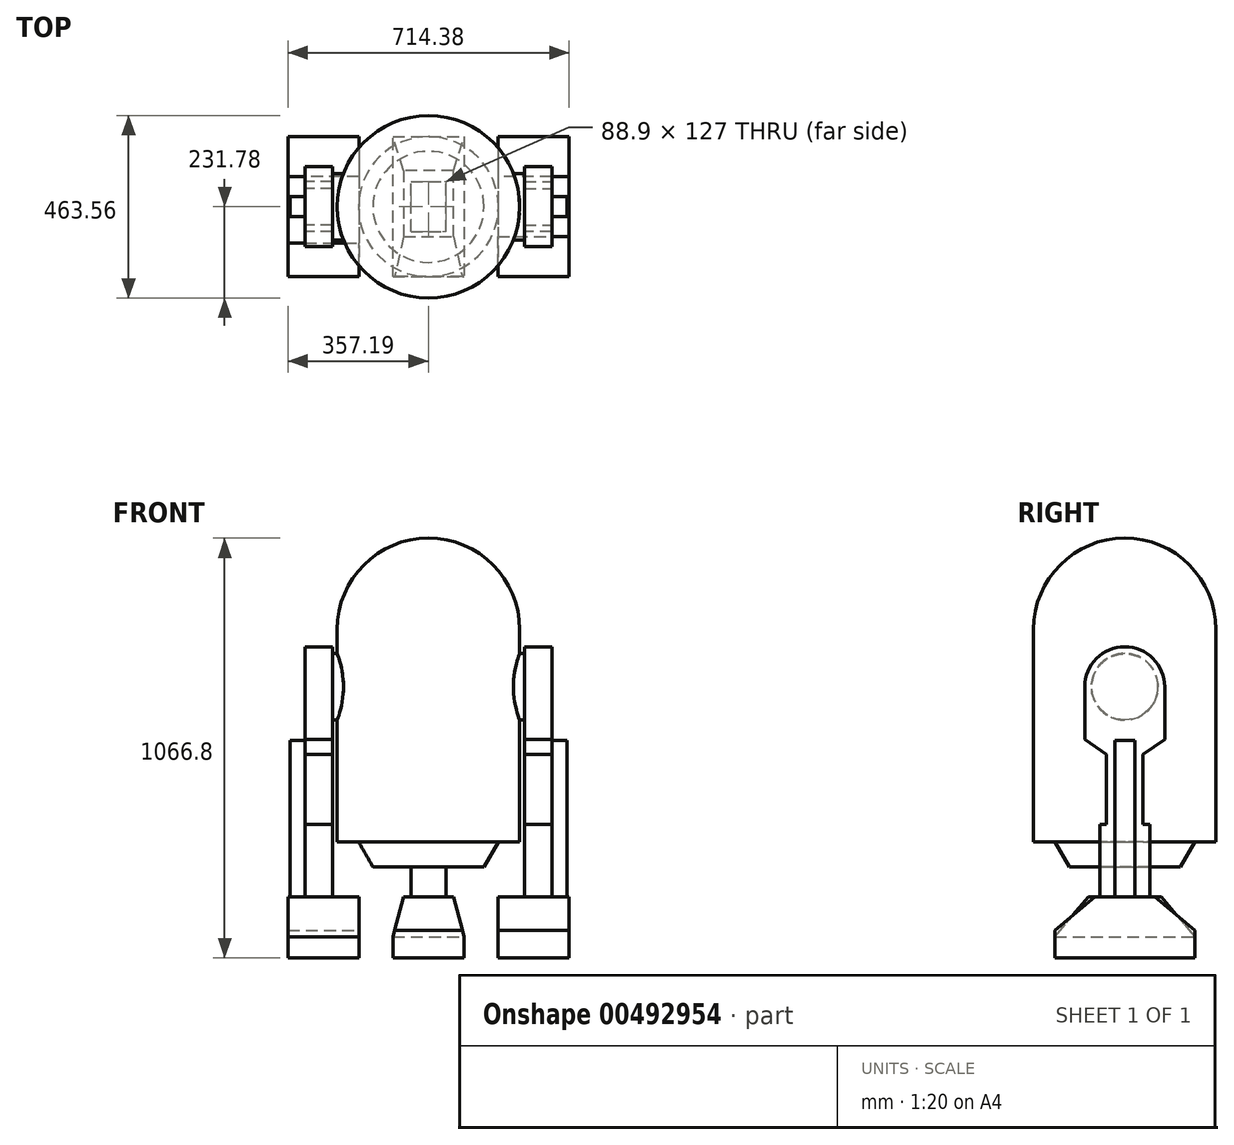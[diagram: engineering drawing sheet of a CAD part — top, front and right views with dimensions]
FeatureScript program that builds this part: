
annotation { "Feature Type Name" : "Feature", "Feature Type Description" : "" }
export const myFeature = defineFeature(function(context is Context, id is Id, definition is map)
    precondition{}
    {
        {
            var Q0;
            Q0=qCreatedBy(makeId("Top.planeOp"),FACE);
            var sketch = newSketch(context, id + "F0", { "sketchPlane" : qUnion([Q0])});
            skCircle(sketch, "E0", {"center": v(0, 0) * mm, "radius": 231.78 * mm});
            skLineSegment(sketch, "E1.bottom", {"start": v(243.68, 84.58) * mm, "end": v(215.8, 84.58) * mm});
            skLineSegment(sketch, "E1.top", {"start": v(243.68, -84.58) * mm, "end": v(215.8, -84.58) * mm});
            skLineSegment(sketch, "E1.left", {"start": v(243.68, 84.58) * mm, "end": v(243.68, -84.58) * mm});
            skLineSegment(sketch, "E1.right", {"start": v(-243.68, 84.58) * mm, "end": v(-243.68, -84.58) * mm});
            skLineSegment(sketch, "E2.bottom", {"start": v(313.53, 101.6) * mm, "end": v(243.68, 101.6) * mm});
            skLineSegment(sketch, "E2.top", {"start": v(313.53, -101.6) * mm, "end": v(243.68, -101.6) * mm});
            skLineSegment(sketch, "E2.left", {"start": v(313.53, 101.6) * mm, "end": v(313.53, -101.6) * mm});
            skLineSegment(sketch, "E2.right", {"start": v(243.68, 101.6) * mm, "end": v(243.68, -101.6) * mm});
            skPoint(sketch, "E2.middle", {"position": v(278.6, 0) * mm});
            skLineSegment(sketch, "E3.bottom", {"start": v(338.93, -50.8) * mm, "end": v(313.53, -50.8) * mm});
            skLineSegment(sketch, "E3.top", {"start": v(338.93, 50.8) * mm, "end": v(313.53, 50.8) * mm});
            skLineSegment(sketch, "E3.left", {"start": v(338.93, -50.8) * mm, "end": v(338.93, 50.8) * mm});
            skLineSegment(sketch, "E3.right", {"start": v(313.53, -50.8) * mm, "end": v(313.53, 50.8) * mm});
            skPoint(sketch, "E3.middle", {"position": v(326.23, 0) * mm});
            skLineSegment(sketch, "E4.trimOffspring", {"start": v(-215.8, 84.58) * mm, "end": v(-243.68, 84.58) * mm});
            skLineSegment(sketch, "E5.trimOffspring", {"start": v(-215.8, -84.58) * mm, "end": v(-243.68, -84.58) * mm});
            skLineSegment(sketch, "E6.MirrorCS", {"start": v(-243.68, 101.6) * mm, "end": v(-243.68, -101.6) * mm});
            skLineSegment(sketch, "E7.MirrorCS", {"start": v(-313.53, 101.6) * mm, "end": v(-243.68, 101.6) * mm});
            skLineSegment(sketch, "E8.MirrorCS", {"start": v(-313.53, -101.6) * mm, "end": v(-243.68, -101.6) * mm});
            skLineSegment(sketch, "E9.MirrorCS", {"start": v(-313.53, 101.6) * mm, "end": v(-313.53, -101.6) * mm});
            skLineSegment(sketch, "E10.MirrorCS", {"start": v(-338.93, -50.8) * mm, "end": v(-313.53, -50.8) * mm});
            skLineSegment(sketch, "E11.MirrorCS", {"start": v(-338.93, -50.8) * mm, "end": v(-338.93, 50.8) * mm});
            skLineSegment(sketch, "E12.MirrorCS", {"start": v(-338.93, 50.8) * mm, "end": v(-313.53, 50.8) * mm});
            skLineSegment(sketch, "E13", {"start": v(0, 0) * mm, "end": v(0, 231.78) * mm});
            skLineSegment(sketch, "E14", {"start": v(0, 0) * mm, "end": v(0, -231.78) * mm});
            skLineSegment(sketch, "E15", {"start": v(313.53, 0) * mm, "end": v(243.68, 0) * mm});
            skLineSegment(sketch, "E16", {"start": v(-243.68, 0) * mm, "end": v(-313.53, 0) * mm});
            skSolve(sketch);
        }
        {
            var Q0;
            {var subQ0=sQuery(id+"F0.wireOp",EDGE,"E0");var subQ1=makeQuery(id+"F0.imprint","INTERSECT",VERTEX,{"derivedFrom":[subQ0,sQuery(id+"F0.wireOp",EDGE,"E1.bottom")]});Q0=makeQuery(id+"F0.imprint","IMPRINT",FACE,{"disambiguationData":[TD([[makeQuery(id+"F0.imprint","IMPRINT",EDGE,{"disambiguationData":[TD([[subQ1,-1.0]])],"derivedFrom":subQ0}),1.0]])]});}
            var Q1;
            {var subQ3=sQuery(id+"F0.wireOp",EDGE,"E13");Q1=makeQuery(id+"F0.imprint","IMPRINT",FACE,{"disambiguationData":[TD([[makeQuery(id+"F0.imprint","IMPRINT",EDGE,{"derivedFrom":subQ3}),1.0]])]});}
            extrude(context, id + "F1", {"entities" : qUnion([Q0, Q1]), "oppositeDirection" : true, "depth" : 539.75 * mm});
        }
        {
            var Q0;
            {var subQ0=sQuery(id+"F0.wireOp",EDGE,"E13");Q0=makeQuery(id+"F0.imprint","IMPRINT",FACE,{"disambiguationData":[TD([[makeQuery(id+"F0.imprint","IMPRINT",EDGE,{"derivedFrom":subQ0}),-1.0]])]});}
            var Q1;
            Q1=sQuery(id+"F0.wireOp",EDGE,"E14");
            revolve(context, id + "F2", {"operationType" : NewBodyOperationType.ADD, "entities" : qUnion([Q0]), "axis" : qUnion([Q1]), "revolveType" : RevolveType.ONE_DIRECTION, "angle" : 180 * degree});
        }
        {
            var Q0;
            {var subQ2=sQuery(id+"F0.wireOp",EDGE,"E2.top");Q0=makeQuery(id+"F0.imprint","IMPRINT",FACE,{"disambiguationData":[TD([[makeQuery(id+"F0.imprint","IMPRINT",EDGE,{"derivedFrom":subQ2}),-1.0]])]});}
            var Q1;
            {var subQ2=sQuery(id+"F0.wireOp",EDGE,"E2.bottom");Q1=makeQuery(id+"F0.imprint","IMPRINT",FACE,{"disambiguationData":[TD([[makeQuery(id+"F0.imprint","IMPRINT",EDGE,{"derivedFrom":subQ2}),1.0]])]});}
            extrude(context, id + "F3", {"entities" : qUnion([Q0, Q1]), "oppositeDirection" : true, "depth" : 714.38 * mm, "hasSecondDirection" : true, "secondDirectionOppositeDirection" : true, "secondDirectionDepth" : 146.05 * mm});
        }
        {
            var Q0;
            Q0=makeQuery(id+"F3.opExtrude","CAP_FACE",FACE,{"disambiguationData":[OSD([sQuery(id+"F0.wireOp",EDGE,"E2.bottom"),sQuery(id+"F0.wireOp",EDGE,"E2.top"),sQuery(id+"F0.wireOp",EDGE,"E2.left"),sQuery(id+"F0.wireOp",EDGE,"E2.right"),sQuery(id+"F0.wireOp",EDGE,"E3.right")])],"isStart":true});
            var sketch = newSketch(context, id + "F4", { "sketchPlane" : qUnion([Q0])});
            skLineSegment(sketch, "E17", {"start": v(313.53, 0) * mm, "end": v(243.68, 0) * mm});
            skSolve(sketch);
        }
        {
            var Q0;
            {var subQ0=sQuery(id+"F4.wireOp",EDGE,"E17");Q0=makeQuery(id+"F4.imprint","IMPRINT",FACE,{"disambiguationData":[TD([[makeQuery(id+"F4.imprint","IMPRINT",EDGE,{"derivedFrom":subQ0}),1.0]])]});}
            var Q1;
            Q1=sQuery(id+"F4.wireOp",EDGE,"E17");
            revolve(context, id + "F5", {"operationType" : NewBodyOperationType.ADD, "entities" : qUnion([Q0]), "axis" : qUnion([Q1]), "revolveType" : RevolveType.FULL});
        }
        {
            var Q0;
            {var subQ0=sQuery(id+"F0.wireOp",EDGE,"E3.right");var subQ1=sQuery(id+"F0.wireOp",EDGE,"E2.left");Q0=makeQuery(id+"F5.boolean.opBoolean","MERGE",FACE,{"derivedFrom":[makeQuery(id+"F3.opExtrude","SWEPT_FACE",FACE,{"disambiguationData":[OSD([subQ1,subQ0])]}),makeQuery(id+"F5.opRevolve","SWEPT_FACE",FACE,{"disambiguationData":[OSD([subQ1,subQ0])]})]});}
            var sketch = newSketch(context, id + "F6", { "sketchPlane" : qUnion([Q0])});
            skCircle(sketch, "E18", {"center": v(0, -146.05) * mm, "radius": 84.58 * mm});
            skLineSegment(sketch, "E19.bottom", {"start": v(46.04, -317.5) * mm, "end": v(-46.04, -317.5) * mm, "construction": true});
            skLineSegment(sketch, "E19.left", {"start": v(46.04, -317.5) * mm, "end": v(46.04, -495.3) * mm});
            skLineSegment(sketch, "E19.right", {"start": v(-46.04, -317.5) * mm, "end": v(-46.04, -495.3) * mm});
            skPoint(sketch, "E19.middle", {"position": v(0, -406.4) * mm});
            skLineSegment(sketch, "E20", {"start": v(-101.6, -279.4) * mm, "end": v(-46.04, -317.5) * mm});
            skLineSegment(sketch, "E21", {"start": v(101.6, -279.4) * mm, "end": v(46.04, -317.5) * mm});
            skLineSegment(sketch, "E22.bottom", {"start": v(63.5, -495.3) * mm, "end": v(46.04, -495.3) * mm});
            skLineSegment(sketch, "E22.top", {"start": v(63.5, -714.38) * mm, "end": v(-63.5, -714.38) * mm});
            skLineSegment(sketch, "E22.left", {"start": v(63.5, -495.3) * mm, "end": v(63.5, -714.38) * mm});
            skLineSegment(sketch, "E22.right", {"start": v(-63.5, -495.3) * mm, "end": v(-63.5, -714.38) * mm});
            skPoint(sketch, "E22.middle", {"position": v(0, -604.84) * mm});
            skLineSegment(sketch, "E23.trimOffspring", {"start": v(-46.04, -495.3) * mm, "end": v(-63.5, -495.3) * mm});
            skSolve(sketch);
        }
        {
            var Q0;
            Q0=makeQuery(id+"F6.imprint","IMPRINT",FACE,{"disambiguationData":[TD([[makeQuery(id+"F6.imprint","IMPRINT",EDGE,{"derivedFrom":sQuery(id+"F6.wireOp",EDGE,"E19.left")}),1.0]])]});
            var Q1;
            Q1=makeQuery(id+"F6.imprint","IMPRINT",FACE,{"disambiguationData":[TD([[makeQuery(id+"F6.imprint","IMPRINT",EDGE,{"derivedFrom":sQuery(id+"F6.wireOp",EDGE,"E19.right")}),-1.0]])]});
            var Q2;
            {var subQ0=sQuery(id+"F0.wireOp",EDGE,"E2.right");Q2=makeQuery(id+"F5.boolean.opBoolean","MERGE",FACE,{"derivedFrom":[makeQuery(id+"F3.opExtrude","SWEPT_FACE",FACE,{"disambiguationData":[OSD([subQ0])]}),makeQuery(id+"F5.opRevolve","SWEPT_FACE",FACE,{"disambiguationData":[OSD([subQ0])]})]});}
            extrude(context, id + "F7", {"entities" : qUnion([Q0, Q1]), "operationType" : NewBodyOperationType.REMOVE, "endBound" : BoundingType.UP_TO_SURFACE, "oppositeDirection" : true, "endBoundEntityFace" : qUnion([Q2]), "depth" : 25.4 * mm});
        }
        {
            var Q0;
            Q0=makeQuery(id+"F6.imprint","IMPRINT",FACE,{"disambiguationData":[TD([[makeQuery(id+"F6.imprint","IMPRINT",EDGE,{"derivedFrom":sQuery(id+"F6.wireOp",EDGE,"E18")}),-1.0]])]});
            var sketch = newSketch(context, id + "F8", { "sketchPlane" : qUnion([Q0])});
            skLineSegment(sketch, "E24.bottom", {"start": v(25.4, -282.58) * mm, "end": v(-25.4, -282.58) * mm});
            skLineSegment(sketch, "E24.top", {"start": v(25.4, -714.38) * mm, "end": v(-25.4, -714.38) * mm});
            skLineSegment(sketch, "E24.left", {"start": v(25.4, -282.58) * mm, "end": v(25.4, -714.38) * mm});
            skLineSegment(sketch, "E24.right", {"start": v(-25.4, -282.58) * mm, "end": v(-25.4, -714.38) * mm});
            skPoint(sketch, "E24.middle", {"position": v(0, -498.48) * mm});
            skSolve(sketch);
        }
        {
            var Q0;
            Q0=makeQuery(id+"F8.imprint","IMPRINT",FACE,{"disambiguationData":[TD([[makeQuery(id+"F8.imprint","IMPRINT",EDGE,{"derivedFrom":sQuery(id+"F8.wireOp",EDGE,"E24.bottom")}),1.0]])]});
            extrude(context, id + "F9", {"entities" : qUnion([Q0]), "operationType" : NewBodyOperationType.ADD, "depth" : 38.1 * mm});
        }
        {
            var Q0;
            Q0=makeQuery(id+"F3.opExtrude","SWEPT_BODY",BODY,{"disambiguationData":[OSD([sQuery(id+"F0.wireOp",EDGE,"E2.bottom"),sQuery(id+"F0.wireOp",EDGE,"E2.top"),sQuery(id+"F0.wireOp",EDGE,"E2.left"),sQuery(id+"F0.wireOp",EDGE,"E2.right"),sQuery(id+"F0.wireOp",EDGE,"E3.right")])]});
            var Q1;
            Q1=qCreatedBy(makeId("Right.planeOp"),FACE);
            mirror(context, id + "F10", {"entities" : qUnion([Q0]), "mirrorPlane" : qUnion([Q1])});
        }
        {
            var Q0;
            Q0=makeQuery(id+"F6.imprint","IMPRINT",FACE,{"disambiguationData":[TD([[makeQuery(id+"F6.imprint","IMPRINT",EDGE,{"derivedFrom":sQuery(id+"F6.wireOp",EDGE,"E18")}),1.0]])]});
            var Q1;
            Q1=sQuery(id+"F6.wireOp",EDGE,"E18");
            var Q2;
            {var subQ0=sQuery(id+"F0.wireOp",EDGE,"E3.right");var subQ1=sQuery(id+"F0.wireOp",EDGE,"E2.left");Q2=makeQuery(id+"F10.opPattern","COPY",FACE,{"derivedFrom":makeQuery(id+"F5.boolean.opBoolean","MERGE",FACE,{"derivedFrom":[makeQuery(id+"F3.opExtrude","SWEPT_FACE",FACE,{"disambiguationData":[OSD([subQ1,subQ0])]}),makeQuery(id+"F5.opRevolve","SWEPT_FACE",FACE,{"disambiguationData":[OSD([subQ1,subQ0])]})]}),"instanceName":"1"});}
            extrude(context, id + "F11", {"entities" : qUnion([Q0]), "operationType" : NewBodyOperationType.ADD, "surfaceEntities" : qUnion([Q1]), "endBound" : BoundingType.UP_TO_SURFACE, "oppositeDirection" : true, "endBoundEntityFace" : qUnion([Q2]), "depth" : 25.4 * mm});
        }
        {
            var Q0;
            Q0=makeQuery(id+"F1.opExtrude","CAP_FACE",FACE,{"disambiguationData":[OSD([sQuery(id+"F0.wireOp",EDGE,"E0")])],"isStart":false});
            var sketch = newSketch(context, id + "F12", { "sketchPlane" : qUnion([Q0])});
            skCircle(sketch, "E25", {"center": v(0, 0) * mm, "radius": 177.8 * mm});
            skSolve(sketch);
        }
        {
            var Q0;
            Q0=makeQuery(id+"F12.imprint","IMPRINT",FACE,{"disambiguationData":[TD([[makeQuery(id+"F12.imprint","IMPRINT",EDGE,{"derivedFrom":sQuery(id+"F12.wireOp",EDGE,"E25")}),1.0]])]});
            extrude(context, id + "F13", {"entities" : qUnion([Q0]), "operationType" : NewBodyOperationType.ADD, "depth" : 63.5 * mm});
        }
        {
            var Q0;
            Q0=makeQuery(id+"F13.opExtrude","CAP_EDGE",EDGE,{"disambiguationData":[OSD([sQuery(id+"F12.wireOp",EDGE,"E25")])],"isStart":false});
            chamfer(context, id + "F14", {"entities" : qUnion([Q0]), "chamferType" : ChamferType.OFFSET_ANGLE, "width" : 63.5 * mm, "oppositeDirection" : true, "angle" : 30 * degree, "tangentPropagation" : true});
        }
        {
            var Q0;
            Q0=qCreatedBy(makeId("Top.planeOp"),FACE);
            cPlane(context, id + "F15", {"entities" : qUnion([Q0]), "cplaneType" : CPlaneType.OFFSET, "offset" : 835.02 * mm, "oppositeDirection" : true, "width" : 152.4 * mm, "height" : 152.4 * mm});
        }
        {
            var Q0;
            Q0=qCreatedBy(id+"F15.planeOp",FACE);
            var sketch = newSketch(context, id + "F16", { "sketchPlane" : qUnion([Q0])});
            skLineSegment(sketch, "E26.bottom", {"start": v(-90.49, 177.8) * mm, "end": v(90.49, 177.8) * mm});
            skLineSegment(sketch, "E26.top", {"start": v(-90.49, -177.8) * mm, "end": v(90.49, -177.8) * mm});
            skLineSegment(sketch, "E26.left", {"start": v(-90.49, 177.8) * mm, "end": v(-90.49, -177.8) * mm});
            skLineSegment(sketch, "E26.right", {"start": v(90.49, 177.8) * mm, "end": v(90.49, -177.8) * mm});
            skPoint(sketch, "E26.middle", {"position": v(0, 0) * mm});
            skLineSegment(sketch, "E27.1.0.0", {"start": v(176.21, -177.8) * mm, "end": v(357.19, -177.8) * mm});
            skLineSegment(sketch, "E27.1.0.1", {"start": v(176.21, 177.8) * mm, "end": v(176.21, -177.8) * mm});
            skLineSegment(sketch, "E27.1.0.2", {"start": v(357.19, 177.8) * mm, "end": v(357.19, -177.8) * mm});
            skLineSegment(sketch, "E27.1.0.3", {"start": v(176.21, 177.8) * mm, "end": v(357.19, 177.8) * mm});
            skLineSegment(sketch, "E27.direction1", {"start": v(-90.49, -177.8) * mm, "end": v(176.21, -177.8) * mm, "construction": true});
            skLineSegment(sketch, "E28", {"start": v(266.7, -177.8) * mm, "end": v(266.7, 177.8) * mm, "construction": true});
            skLineSegment(sketch, "E29", {"start": v(0, -177.8) * mm, "end": v(0, 177.8) * mm, "construction": true});
            skLineSegment(sketch, "E30.MirrorCS", {"start": v(-176.21, 177.8) * mm, "end": v(-176.21, -177.8) * mm});
            skLineSegment(sketch, "E31.MirrorCS", {"start": v(-176.21, -177.8) * mm, "end": v(-357.19, -177.8) * mm});
            skLineSegment(sketch, "E32.MirrorCS", {"start": v(-357.19, 177.8) * mm, "end": v(-357.19, -177.8) * mm});
            skLineSegment(sketch, "E33.MirrorCS", {"start": v(-176.21, 177.8) * mm, "end": v(-357.19, 177.8) * mm});
            skSolve(sketch);
        }
        {
            var Q0;
            Q0=makeQuery(id+"F16.imprint","IMPRINT",FACE,{"disambiguationData":[TD([[makeQuery(id+"F16.imprint","IMPRINT",EDGE,{"derivedFrom":sQuery(id+"F16.wireOp",EDGE,"E30.MirrorCS")}),-1.0]])]});
            var Q1;
            Q1=makeQuery(id+"F16.imprint","IMPRINT",FACE,{"disambiguationData":[TD([[makeQuery(id+"F16.imprint","IMPRINT",EDGE,{"derivedFrom":sQuery(id+"F16.wireOp",EDGE,"E26.bottom")}),-1.0]])]});
            var Q2;
            Q2=makeQuery(id+"F16.imprint","IMPRINT",FACE,{"disambiguationData":[TD([[makeQuery(id+"F16.imprint","IMPRINT",EDGE,{"derivedFrom":sQuery(id+"F16.wireOp",EDGE,"E27.1.0.0")}),1.0]])]});
            extrude(context, id + "F17", {"entities" : qUnion([Q0, Q1, Q2]), "operationType" : NewBodyOperationType.ADD, "depth" : 155.57 * mm});
        }
        {
            var Q0;
            Q0=makeQuery(id+"F17.opExtrude","CAP_FACE",FACE,{"disambiguationData":[OSD([sQuery(id+"F16.wireOp",EDGE,"E26.bottom"),sQuery(id+"F16.wireOp",EDGE,"E26.top"),sQuery(id+"F16.wireOp",EDGE,"E26.left"),sQuery(id+"F16.wireOp",EDGE,"E26.right")])],"isStart":false});
            var sketch = newSketch(context, id + "F18", { "sketchPlane" : qUnion([Q0])});
            skLineSegment(sketch, "E34.bottom", {"start": v(44.45, 63.5) * mm, "end": v(-44.45, 63.5) * mm});
            skLineSegment(sketch, "E34.top", {"start": v(44.45, -63.5) * mm, "end": v(-44.45, -63.5) * mm});
            skLineSegment(sketch, "E34.left", {"start": v(44.45, 63.5) * mm, "end": v(44.45, -63.5) * mm});
            skLineSegment(sketch, "E34.right", {"start": v(-44.45, 63.5) * mm, "end": v(-44.45, -63.5) * mm});
            skPoint(sketch, "E34.middle", {"position": v(0, 0) * mm});
            skSolve(sketch);
        }
        {
            var Q0;
            Q0=makeQuery(id+"F18.imprint","IMPRINT",FACE,{"disambiguationData":[TD([[makeQuery(id+"F18.imprint","IMPRINT",EDGE,{"derivedFrom":sQuery(id+"F18.wireOp",EDGE,"E34.bottom")}),1.0]])]});
            var Q1;
            Q1=makeQuery(id+"F13.opExtrude","CAP_FACE",FACE,{"disambiguationData":[OSD([sQuery(id+"F12.wireOp",EDGE,"E25")])],"isStart":false});
            extrude(context, id + "F19", {"entities" : qUnion([Q0]), "operationType" : NewBodyOperationType.ADD, "endBound" : BoundingType.UP_TO_SURFACE, "endBoundEntityFace" : qUnion([Q1]), "depth" : 25.4 * mm});
        }
        {
            var Q0;
            Q0=makeQuery(id+"F17.opExtrude","CAP_EDGE",EDGE,{"disambiguationData":[OSD([sQuery(id+"F16.wireOp",EDGE,"E27.1.0.0")])],"isStart":false});
            var Q1;
            Q1=makeQuery(id+"F17.opExtrude","CAP_EDGE",EDGE,{"disambiguationData":[OSD([sQuery(id+"F16.wireOp",EDGE,"E31.MirrorCS")])],"isStart":false});
            var Q2;
            Q2=makeQuery(id+"F17.opExtrude","CAP_EDGE",EDGE,{"disambiguationData":[OSD([sQuery(id+"F16.wireOp",EDGE,"E33.MirrorCS")])],"isStart":false});
            var Q3;
            Q3=makeQuery(id+"F17.opExtrude","CAP_EDGE",EDGE,{"disambiguationData":[OSD([sQuery(id+"F16.wireOp",EDGE,"E27.1.0.3")])],"isStart":false});
            var Q4;
            Q4=makeQuery(id+"F17.opExtrude","CAP_EDGE",EDGE,{"disambiguationData":[OSD([sQuery(id+"F16.wireOp",EDGE,"E26.bottom")])],"isStart":false});
            var Q5;
            Q5=makeQuery(id+"F17.opExtrude","CAP_EDGE",EDGE,{"disambiguationData":[OSD([sQuery(id+"F16.wireOp",EDGE,"E26.top")])],"isStart":false});
            chamfer(context, id + "F20", {"entities" : qUnion([Q0, Q1, Q2, Q3, Q4, Q5]), "chamferType" : ChamferType.OFFSET_ANGLE, "width" : 101.6 * mm, "oppositeDirection" : false, "angle" : 40 * degree, "tangentPropagation" : true});
        }
        {
            var Q0;
            Q0=makeQuery(id+"F17.opExtrude","CAP_EDGE",EDGE,{"disambiguationData":[OSD([sQuery(id+"F16.wireOp",EDGE,"E26.left")])],"isStart":false});
            var Q1;
            Q1=makeQuery(id+"F17.opExtrude","CAP_EDGE",EDGE,{"disambiguationData":[OSD([sQuery(id+"F16.wireOp",EDGE,"E26.right")])],"isStart":false});
            chamfer(context, id + "F21", {"entities" : qUnion([Q0, Q1]), "chamferType" : ChamferType.OFFSET_ANGLE, "width" : 101.6 * mm, "oppositeDirection" : true, "angle" : 15 * degree});
        }
        {
            var Q0;
            Q0=qCreatedBy(id+"F15.planeOp",FACE);
            var sketch = newSketch(context, id + "F22", { "sketchPlane" : qUnion([Q0])});
            skLineSegment(sketch, "E35.bottom", {"start": v(406.4, -292.1) * mm, "end": v(-406.4, -292.1) * mm});
            skLineSegment(sketch, "E35.top", {"start": v(406.4, 292.1) * mm, "end": v(-406.4, 292.1) * mm});
            skLineSegment(sketch, "E35.left", {"start": v(406.4, -292.1) * mm, "end": v(406.4, 292.1) * mm});
            skLineSegment(sketch, "E35.right", {"start": v(-406.4, -292.1) * mm, "end": v(-406.4, 292.1) * mm});
            skPoint(sketch, "E35.middle", {"position": v(0, 0) * mm});
            skLineSegment(sketch, "E36", {"start": v(-406.4, -228.6) * mm, "end": v(-368.3, -228.6) * mm});
            skLineSegment(sketch, "E37", {"start": v(-368.3, -228.6) * mm, "end": v(-368.3, -292.1) * mm});
            skLineSegment(sketch, "E38", {"start": v(0, -292.1) * mm, "end": v(0, 292.1) * mm, "construction": true});
            skLineSegment(sketch, "E39", {"start": v(406.4, 0) * mm, "end": v(-406.4, 0) * mm, "construction": true});
            skLineSegment(sketch, "E40.MirrorCS", {"start": v(368.3, -228.6) * mm, "end": v(368.3, -292.1) * mm});
            skLineSegment(sketch, "E41.MirrorCS", {"start": v(406.4, -228.6) * mm, "end": v(368.3, -228.6) * mm});
            skLineSegment(sketch, "E42.MirrorCS", {"start": v(-406.4, 228.6) * mm, "end": v(-368.3, 228.6) * mm});
            skLineSegment(sketch, "E43.MirrorCS", {"start": v(-368.3, 228.6) * mm, "end": v(-368.3, 292.1) * mm});
            skLineSegment(sketch, "E44.MirrorCS", {"start": v(406.4, 228.6) * mm, "end": v(368.3, 228.6) * mm});
            skLineSegment(sketch, "E45.MirrorCS", {"start": v(368.3, 228.6) * mm, "end": v(368.3, 292.1) * mm});
            skLineSegment(sketch, "E46", {"start": v(368.3, 285.75) * mm, "end": v(-368.3, 285.75) * mm});
            skLineSegment(sketch, "E47", {"start": v(-400.05, 228.6) * mm, "end": v(-400.05, -228.6) * mm});
            skLineSegment(sketch, "E48", {"start": v(-135.56, 292.1) * mm, "end": v(-135.56, 285.75) * mm, "construction": true});
            skLineSegment(sketch, "E49", {"start": v(-400.05, 178.52) * mm, "end": v(-406.4, 178.52) * mm, "construction": true});
            skLineSegment(sketch, "E50.MirrorCS", {"start": v(368.3, -285.75) * mm, "end": v(-368.3, -285.75) * mm});
            skLineSegment(sketch, "E51.MirrorCS", {"start": v(400.05, 228.6) * mm, "end": v(400.05, -228.6) * mm});
            skSolve(sketch);
        }
        {
            var Q0;
            {var subQ4=sQuery(id+"F22.wireOp",EDGE,"E44.MirrorCS");Q0=makeQuery(id+"F22.imprint","IMPRINT",FACE,{"disambiguationData":[TD([[makeQuery(id+"F22.imprint","IMPRINT",EDGE,{"derivedFrom":subQ4}),-1.0]])]});}
            var Q1;
            {var subQ3=sQuery(id+"F22.wireOp",EDGE,"E40.MirrorCS");Q1=makeQuery(id+"F22.imprint","IMPRINT",FACE,{"disambiguationData":[TD([[makeQuery(id+"F22.imprint","IMPRINT",EDGE,{"derivedFrom":subQ3}),1.0]])]});}
            var Q2;
            {var subQ4=sQuery(id+"F22.wireOp",EDGE,"E42.MirrorCS");Q2=makeQuery(id+"F22.imprint","IMPRINT",FACE,{"disambiguationData":[TD([[makeQuery(id+"F22.imprint","IMPRINT",EDGE,{"derivedFrom":subQ4}),1.0]])]});}
            var Q3;
            {var subQ4=sQuery(id+"F22.wireOp",EDGE,"E36");Q3=makeQuery(id+"F22.imprint","IMPRINT",FACE,{"disambiguationData":[TD([[makeQuery(id+"F22.imprint","IMPRINT",EDGE,{"derivedFrom":subQ4}),-1.0]])]});}
            extrude(context, id + "F23", {"entities" : qUnion([Q0, Q1, Q2, Q3]), "depth" : 1136.65 * mm, "hasSecondDirection" : true, "secondDirectionOppositeDirection" : true, "secondDirectionDepth" : 101.6 * mm});
        }
        {
            var Q0;
            {var subQ4=sQuery(id+"F22.wireOp",EDGE,"E36");Q0=makeQuery(id+"F22.imprint","IMPRINT",FACE,{"disambiguationData":[TD([[makeQuery(id+"F22.imprint","IMPRINT",EDGE,{"derivedFrom":subQ4}),1.0]])]});}
            var Q1;
            {var subQ1=sQuery(id+"F22.wireOp",EDGE,"E46");Q1=makeQuery(id+"F22.imprint","IMPRINT",FACE,{"disambiguationData":[TD([[makeQuery(id+"F22.imprint","IMPRINT",EDGE,{"derivedFrom":subQ1}),1.0]])]});}
            var Q2;
            {var subQ5=sQuery(id+"F22.wireOp",EDGE,"E46");Q2=makeQuery(id+"F22.imprint","IMPRINT",FACE,{"disambiguationData":[TD([[makeQuery(id+"F22.imprint","IMPRINT",EDGE,{"derivedFrom":subQ5}),-1.0]])]});}
            var Q3;
            {var subQ5=sQuery(id+"F22.wireOp",EDGE,"E50.MirrorCS");Q3=makeQuery(id+"F22.imprint","IMPRINT",FACE,{"disambiguationData":[TD([[makeQuery(id+"F22.imprint","IMPRINT",EDGE,{"derivedFrom":subQ5}),1.0]])]});}
            var Q4;
            {var subQ5=sQuery(id+"F22.wireOp",EDGE,"E51.MirrorCS");Q4=makeQuery(id+"F22.imprint","IMPRINT",FACE,{"disambiguationData":[TD([[makeQuery(id+"F22.imprint","IMPRINT",EDGE,{"derivedFrom":subQ5}),1.0]])]});}
            extrude(context, id + "F24", {"entities" : qUnion([Q0, Q1, Q2, Q3, Q4]), "oppositeDirection" : true, "depth" : 12.7 * mm});
        }
        {
            var Q0;
            {var subQ5=sQuery(id+"F22.wireOp",EDGE,"E46");Q0=makeQuery(id+"F22.imprint","IMPRINT",FACE,{"disambiguationData":[TD([[makeQuery(id+"F22.imprint","IMPRINT",EDGE,{"derivedFrom":subQ5}),-1.0]])]});}
            var Q1;
            {var subQ5=sQuery(id+"F22.wireOp",EDGE,"E51.MirrorCS");Q1=makeQuery(id+"F22.imprint","IMPRINT",FACE,{"disambiguationData":[TD([[makeQuery(id+"F22.imprint","IMPRINT",EDGE,{"derivedFrom":subQ5}),1.0]])]});}
            var Q2;
            {var subQ5=sQuery(id+"F22.wireOp",EDGE,"E50.MirrorCS");Q2=makeQuery(id+"F22.imprint","IMPRINT",FACE,{"disambiguationData":[TD([[makeQuery(id+"F22.imprint","IMPRINT",EDGE,{"derivedFrom":subQ5}),1.0]])]});}
            var Q3;
            {var subQ5=sQuery(id+"F22.wireOp",EDGE,"E47");Q3=makeQuery(id+"F22.imprint","IMPRINT",FACE,{"disambiguationData":[TD([[makeQuery(id+"F22.imprint","IMPRINT",EDGE,{"derivedFrom":subQ5}),-1.0]])]});}
            var Q4;
            Q4=makeQuery(id+"F23.opExtrude","CAP_FACE",FACE,{"disambiguationData":[OSD([sQuery(id+"F22.wireOp",EDGE,"E35.top"),sQuery(id+"F22.wireOp",EDGE,"E35.left"),sQuery(id+"F22.wireOp",EDGE,"E44.MirrorCS"),sQuery(id+"F22.wireOp",EDGE,"E45.MirrorCS")])],"isStart":false});
            extrude(context, id + "F25", {"entities" : qUnion([Q0, Q1, Q2, Q3]), "endBound" : BoundingType.UP_TO_SURFACE, "endBoundEntityFace" : qUnion([Q4]), "depth" : 25.4 * mm});
        }
        {
            var Q0;
            Q0=makeQuery(id+"F23.opExtrude","SWEPT_FACE",FACE,{"disambiguationData":[OSD([sQuery(id+"F22.wireOp",EDGE,"E41.MirrorCS")])]});
            var sketch = newSketch(context, id + "F26", { "sketchPlane" : qUnion([Q0])});
            skLineSegment(sketch, "E52", {"start": v(-406.4, -847.73) * mm, "end": v(-368.3, -847.73) * mm});
            skLineSegment(sketch, "E53", {"start": v(-406.4, -936.63) * mm, "end": v(-368.3, -936.63) * mm});
            skSolve(sketch);
        }
        {
            var Q0;
            {var subQ0=sQuery(id+"F26.wireOp",EDGE,"E52");Q0=makeQuery(id+"F26.imprint","IMPRINT",FACE,{"disambiguationData":[TD([[makeQuery(id+"F26.imprint","IMPRINT",EDGE,{"derivedFrom":subQ0}),-1.0]])]});}
            var Q1;
            Q1=makeQuery(id+"F23.opExtrude","SWEPT_FACE",FACE,{"disambiguationData":[OSD([sQuery(id+"F22.wireOp",EDGE,"E44.MirrorCS")])]});
            extrude(context, id + "F27", {"entities" : qUnion([Q0]), "endBound" : BoundingType.UP_TO_SURFACE, "endBoundEntityFace" : qUnion([Q1]), "depth" : 25.4 * mm});
        }
        {
            var Q0;
            Q0=makeQuery(id+"F27.opExtrude","SWEPT_BODY",BODY,{"disambiguationData":[OSD([sQuery(id+"F22.wireOp",EDGE,"E35.left"),sQuery(id+"F22.wireOp",EDGE,"E40.MirrorCS"),sQuery(id+"F22.wireOp",EDGE,"E41.MirrorCS"),sQuery(id+"F26.wireOp",EDGE,"E52"),sQuery(id+"F26.wireOp",EDGE,"E53")])]});
            var Q1;
            Q1=qCreatedBy(makeId("Right.planeOp"),FACE);
            mirror(context, id + "F28", {"entities" : qUnion([Q0]), "mirrorPlane" : qUnion([Q1])});
        }
        {
            var Q0;
            Q0=makeQuery(id+"F23.opExtrude","CAP_FACE",FACE,{"disambiguationData":[OSD([sQuery(id+"F22.wireOp",EDGE,"E35.top"),sQuery(id+"F22.wireOp",EDGE,"E35.left"),sQuery(id+"F22.wireOp",EDGE,"E44.MirrorCS"),sQuery(id+"F22.wireOp",EDGE,"E45.MirrorCS")])],"isStart":false});
            var sketch = newSketch(context, id + "F29", { "sketchPlane" : qUnion([Q0])});
            skLineSegment(sketch, "E54.bottom", {"start": v(406.4, 292.1) * mm, "end": v(-406.4, 292.1) * mm});
            skLineSegment(sketch, "E54.top", {"start": v(406.4, -292.1) * mm, "end": v(-406.4, -292.1) * mm});
            skLineSegment(sketch, "E54.left", {"start": v(406.4, 292.1) * mm, "end": v(406.4, -292.1) * mm});
            skLineSegment(sketch, "E54.right", {"start": v(-406.4, 292.1) * mm, "end": v(-406.4, -292.1) * mm});
            skPoint(sketch, "E54.middle", {"position": v(0, 0) * mm});
            skSolve(sketch);
        }
        {
            var Q0;
            {var subQ3=sQuery(id+"F29.wireOp",EDGE,"E54.top");Q0=makeQuery(id+"F29.imprint","IMPRINT",FACE,{"disambiguationData":[TD([[makeQuery(id+"F29.imprint","IMPRINT",EDGE,{"derivedFrom":subQ3}),-1.0]])]});}
            var Q1;
            {var subQ4=makeQuery(id+"F23.opExtrude","CAP_EDGE",EDGE,{"disambiguationData":[OSD([sQuery(id+"F22.wireOp",EDGE,"E44.MirrorCS")])],"isStart":false});Q1=makeQuery(id+"F29.imprint","IMPRINT",FACE,{"disambiguationData":[TD([[makeQuery(id+"F29.imprint","IMPRINT",EDGE,{"derivedFrom":subQ4}),-1.0]])]});}
            extrude(context, id + "F30", {"entities" : qUnion([Q0, Q1]), "depth" : 6.35 * mm});
        }
        {
            var Q0;
            Q0=makeQuery(id+"F23.opExtrude","CAP_FACE",FACE,{"disambiguationData":[OSD([sQuery(id+"F22.wireOp",EDGE,"E35.top"),sQuery(id+"F22.wireOp",EDGE,"E35.left"),sQuery(id+"F22.wireOp",EDGE,"E44.MirrorCS"),sQuery(id+"F22.wireOp",EDGE,"E45.MirrorCS")])],"isStart":true});
            var sketch = newSketch(context, id + "F31", { "sketchPlane" : qUnion([Q0])});
            skLineSegment(sketch, "E55.bottom", {"start": v(-406.4, -292.1) * mm, "end": v(406.4, -292.1) * mm});
            skLineSegment(sketch, "E55.top", {"start": v(-406.4, -177.8) * mm, "end": v(406.4, -177.8) * mm});
            skLineSegment(sketch, "E55.left", {"start": v(-406.4, -292.1) * mm, "end": v(-406.4, -177.8) * mm});
            skLineSegment(sketch, "E55.right", {"start": v(406.4, -292.1) * mm, "end": v(406.4, -177.8) * mm});
            skPoint(sketch, "E55.middle", {"position": v(0, -234.95) * mm});
            skLineSegment(sketch, "E56.MirrorCS", {"start": v(-406.4, 177.8) * mm, "end": v(406.4, 177.8) * mm});
            skLineSegment(sketch, "E57.MirrorCS", {"start": v(406.4, 292.1) * mm, "end": v(406.4, 177.8) * mm});
            skLineSegment(sketch, "E58.MirrorCS", {"start": v(-406.4, 292.1) * mm, "end": v(406.4, 292.1) * mm});
            skLineSegment(sketch, "E59.MirrorCS", {"start": v(-406.4, 292.1) * mm, "end": v(-406.4, 177.8) * mm});
            skSolve(sketch);
        }
        {
            var Q0;
            {var subQ2=sQuery(id+"F31.wireOp",EDGE,"E55.top");Q0=makeQuery(id+"F31.imprint","IMPRINT",FACE,{"disambiguationData":[TD([[makeQuery(id+"F31.imprint","IMPRINT",EDGE,{"derivedFrom":subQ2}),-1.0]])]});}
            var Q1;
            Q1=makeQuery(id+"F31.imprint","IMPRINT",FACE,{"disambiguationData":[TD([[makeQuery(id+"F31.imprint","IMPRINT",EDGE,{"derivedFrom":sQuery(id+"F31.wireOp",EDGE,"E56.MirrorCS")}),1.0]])]});
            var Q2;
            {var subQ4=makeQuery(id+"F23.opExtrude","CAP_EDGE",EDGE,{"disambiguationData":[OSD([sQuery(id+"F22.wireOp",EDGE,"E44.MirrorCS")])],"isStart":true});Q2=makeQuery(id+"F31.imprint","IMPRINT",FACE,{"disambiguationData":[TD([[makeQuery(id+"F31.imprint","IMPRINT",EDGE,{"derivedFrom":subQ4}),1.0]])]});}
            extrude(context, id + "F32", {"entities" : qUnion([Q0, Q1, Q2]), "depth" : 12.7 * mm});
        }
        {
            var Q0;
            Q0=makeQuery(id+"F24.opExtrude","CAP_FACE",FACE,{"disambiguationData":[OSD([sQuery(id+"F22.wireOp",EDGE,"E35.bottom"),sQuery(id+"F22.wireOp",EDGE,"E35.top"),sQuery(id+"F22.wireOp",EDGE,"E35.left"),sQuery(id+"F22.wireOp",EDGE,"E35.right"),sQuery(id+"F22.wireOp",EDGE,"E36"),sQuery(id+"F22.wireOp",EDGE,"E37"),sQuery(id+"F22.wireOp",EDGE,"E40.MirrorCS"),sQuery(id+"F22.wireOp",EDGE,"E41.MirrorCS"),sQuery(id+"F22.wireOp",EDGE,"E42.MirrorCS"),sQuery(id+"F22.wireOp",EDGE,"E43.MirrorCS"),sQuery(id+"F22.wireOp",EDGE,"E44.MirrorCS"),sQuery(id+"F22.wireOp",EDGE,"E45.MirrorCS")])],"isStart":false});
            var sketch = newSketch(context, id + "F33", { "sketchPlane" : qUnion([Q0])});
            skLineSegment(sketch, "E60.bottom", {"start": v(76.2, -292.1) * mm, "end": v(38.1, -292.1) * mm});
            skLineSegment(sketch, "E60.top", {"start": v(76.2, 292.1) * mm, "end": v(38.1, 292.1) * mm});
            skLineSegment(sketch, "E60.left", {"start": v(76.2, -292.1) * mm, "end": v(76.2, 292.1) * mm});
            skLineSegment(sketch, "E60.right", {"start": v(38.1, -292.1) * mm, "end": v(38.1, 292.1) * mm});
            skPoint(sketch, "E60.middle", {"position": v(57.15, 0) * mm});
            skLineSegment(sketch, "E61.MirrorCS", {"start": v(-38.1, -292.1) * mm, "end": v(-38.1, 292.1) * mm});
            skLineSegment(sketch, "E62.MirrorCS", {"start": v(-76.2, -292.1) * mm, "end": v(-76.2, 292.1) * mm});
            skSolve(sketch);
        }
        {
            var Q0;
            Q0=makeQuery(id+"F33.imprint","IMPRINT",FACE,{"disambiguationData":[TD([[makeQuery(id+"F33.imprint","IMPRINT",EDGE,{"derivedFrom":sQuery(id+"F33.wireOp",EDGE,"E60.bottom")}),-1.0]])]});
            var Q1;
            {var subQ0=sQuery(id+"F33.wireOp",EDGE,"E61.MirrorCS");Q1=makeQuery(id+"F33.imprint","IMPRINT",FACE,{"disambiguationData":[TD([[makeQuery(id+"F33.imprint","IMPRINT",EDGE,{"derivedFrom":subQ0}),1.0]])]});}
            var Q2;
            Q2=makeQuery(id+"F23.opExtrude","CAP_FACE",FACE,{"disambiguationData":[OSD([sQuery(id+"F22.wireOp",EDGE,"E35.top"),sQuery(id+"F22.wireOp",EDGE,"E35.left"),sQuery(id+"F22.wireOp",EDGE,"E44.MirrorCS"),sQuery(id+"F22.wireOp",EDGE,"E45.MirrorCS")])],"isStart":true});
            extrude(context, id + "F34", {"entities" : qUnion([Q0, Q1]), "endBound" : BoundingType.UP_TO_SURFACE, "endBoundEntityFace" : qUnion([Q2]), "depth" : 25.4 * mm});
        }
        {
            var Q0;
            Q0=makeQuery(id+"F23.opExtrude","SWEPT_FACE",FACE,{"disambiguationData":[OSD([sQuery(id+"F22.wireOp",EDGE,"E45.MirrorCS")])]});
            var sketch = newSketch(context, id + "F35", { "sketchPlane" : qUnion([Q0])});
            skLineSegment(sketch, "E63.bottom", {"start": v(-247.65, -771.53) * mm, "end": v(-285.75, -771.53) * mm});
            skLineSegment(sketch, "E63.top", {"start": v(-247.65, -835.03) * mm, "end": v(-285.75, -835.03) * mm});
            skLineSegment(sketch, "E63.left", {"start": v(-247.65, -771.53) * mm, "end": v(-247.65, -835.03) * mm});
            skLineSegment(sketch, "E63.right", {"start": v(-285.75, -771.53) * mm, "end": v(-285.75, -835.03) * mm});
            skPoint(sketch, "E63.middle", {"position": v(-266.7, -803.28) * mm});
            skSolve(sketch);
        }
        {
            var Q0;
            Q0=makeQuery(id+"F35.imprint","IMPRINT",FACE,{"disambiguationData":[TD([[makeQuery(id+"F35.imprint","IMPRINT",EDGE,{"derivedFrom":sQuery(id+"F35.wireOp",EDGE,"E63.bottom")}),1.0]])]});
            var Q1;
            Q1=makeQuery(id+"F23.opExtrude","SWEPT_FACE",FACE,{"disambiguationData":[OSD([sQuery(id+"F22.wireOp",EDGE,"E43.MirrorCS")])]});
            extrude(context, id + "F36", {"entities" : qUnion([Q0]), "endBound" : BoundingType.UP_TO_SURFACE, "endBoundEntityFace" : qUnion([Q1]), "depth" : 25.4 * mm});
        }
        {
            var Q0;
            Q0=makeQuery(id+"F25.opExtrude","SWEPT_EDGE",EDGE,{"disambiguationData":[OSD([sQuery(id+"F22.wireOp",EDGE,"E42.MirrorCS"),sQuery(id+"F22.wireOp",EDGE,"E47")])]});
            cPlane(context, id + "F37", {"entities" : qUnion([Q0]), "cplaneType" : CPlaneType.MID_PLANE, "offset" : 25.4 * mm, "width" : 152.4 * mm, "height" : 152.4 * mm});
        }
        {
            var Q0;
            Q0=makeQuery(id+"F24.opExtrude","CAP_EDGE",EDGE,{"disambiguationData":[OSD([sQuery(id+"F22.wireOp",EDGE,"E35.right")])],"isStart":false});
            cPlane(context, id + "F38", {"entities" : qUnion([Q0]), "cplaneType" : CPlaneType.MID_PLANE, "offset" : 25.4 * mm, "width" : 152.4 * mm, "height" : 152.4 * mm});
        }
        {
            var Q0;
            Q0=makeQuery(id+"F36.opExtrude","SWEPT_BODY",BODY,{"disambiguationData":[OSD([sQuery(id+"F35.wireOp",EDGE,"E63.bottom"),sQuery(id+"F35.wireOp",EDGE,"E63.top"),sQuery(id+"F35.wireOp",EDGE,"E63.left"),sQuery(id+"F35.wireOp",EDGE,"E63.right")])]});
            var Q1;
            Q1=qCreatedBy(id+"F37.planeOp",FACE);
            mirror(context, id + "F39", {"entities" : qUnion([Q0]), "mirrorPlane" : qUnion([Q1])});
        }
        {
            var Q0;
            Q0=makeQuery(id+"F39.opPattern","COPY",BODY,{"derivedFrom":makeQuery(id+"F36.opExtrude","SWEPT_BODY",BODY,{"disambiguationData":[OSD([sQuery(id+"F35.wireOp",EDGE,"E63.bottom"),sQuery(id+"F35.wireOp",EDGE,"E63.top"),sQuery(id+"F35.wireOp",EDGE,"E63.left"),sQuery(id+"F35.wireOp",EDGE,"E63.right")])]}),"instanceName":"1"});
            var Q1;
            Q1=makeQuery(id+"F36.opExtrude","SWEPT_BODY",BODY,{"disambiguationData":[OSD([sQuery(id+"F35.wireOp",EDGE,"E63.bottom"),sQuery(id+"F35.wireOp",EDGE,"E63.top"),sQuery(id+"F35.wireOp",EDGE,"E63.left"),sQuery(id+"F35.wireOp",EDGE,"E63.right")])]});
            var Q2;
            Q2=qCreatedBy(id+"F38.planeOp",FACE);
            mirror(context, id + "F40", {"entities" : qUnion([Q0, Q1]), "mirrorPlane" : qUnion([Q2])});
        }
        {
            var Q0;
            Q0=makeQuery(id+"F23.opExtrude","SWEPT_BODY",BODY,{"disambiguationData":[OSD([sQuery(id+"F22.wireOp",EDGE,"E35.bottom"),sQuery(id+"F22.wireOp",EDGE,"E35.left"),sQuery(id+"F22.wireOp",EDGE,"E40.MirrorCS"),sQuery(id+"F22.wireOp",EDGE,"E41.MirrorCS")])]});
            var Q1;
            Q1=makeQuery(id+"F23.opExtrude","SWEPT_BODY",BODY,{"disambiguationData":[OSD([sQuery(id+"F22.wireOp",EDGE,"E35.bottom"),sQuery(id+"F22.wireOp",EDGE,"E35.right"),sQuery(id+"F22.wireOp",EDGE,"E36"),sQuery(id+"F22.wireOp",EDGE,"E37")])]});
            var Q2;
            Q2=makeQuery(id+"F23.opExtrude","SWEPT_BODY",BODY,{"disambiguationData":[OSD([sQuery(id+"F22.wireOp",EDGE,"E35.top"),sQuery(id+"F22.wireOp",EDGE,"E35.left"),sQuery(id+"F22.wireOp",EDGE,"E44.MirrorCS"),sQuery(id+"F22.wireOp",EDGE,"E45.MirrorCS")])]});
            var Q3;
            Q3=makeQuery(id+"F23.opExtrude","SWEPT_BODY",BODY,{"disambiguationData":[OSD([sQuery(id+"F22.wireOp",EDGE,"E35.top"),sQuery(id+"F22.wireOp",EDGE,"E35.right"),sQuery(id+"F22.wireOp",EDGE,"E42.MirrorCS"),sQuery(id+"F22.wireOp",EDGE,"E43.MirrorCS")])]});
            var Q4;
            Q4=makeQuery(id+"F24.opExtrude","SWEPT_BODY",BODY,{"disambiguationData":[OSD([sQuery(id+"F22.wireOp",EDGE,"E35.bottom"),sQuery(id+"F22.wireOp",EDGE,"E35.top"),sQuery(id+"F22.wireOp",EDGE,"E35.left"),sQuery(id+"F22.wireOp",EDGE,"E35.right"),sQuery(id+"F22.wireOp",EDGE,"E36"),sQuery(id+"F22.wireOp",EDGE,"E37"),sQuery(id+"F22.wireOp",EDGE,"E40.MirrorCS"),sQuery(id+"F22.wireOp",EDGE,"E41.MirrorCS"),sQuery(id+"F22.wireOp",EDGE,"E42.MirrorCS"),sQuery(id+"F22.wireOp",EDGE,"E43.MirrorCS"),sQuery(id+"F22.wireOp",EDGE,"E44.MirrorCS"),sQuery(id+"F22.wireOp",EDGE,"E45.MirrorCS")])]});
            var Q5;
            Q5=makeQuery(id+"F25.opExtrude","SWEPT_BODY",BODY,{"disambiguationData":[OSD([sQuery(id+"F22.wireOp",EDGE,"E35.bottom"),sQuery(id+"F22.wireOp",EDGE,"E37"),sQuery(id+"F22.wireOp",EDGE,"E40.MirrorCS"),sQuery(id+"F22.wireOp",EDGE,"E50.MirrorCS")])]});
            var Q6;
            Q6=makeQuery(id+"F25.opExtrude","SWEPT_BODY",BODY,{"disambiguationData":[OSD([sQuery(id+"F22.wireOp",EDGE,"E35.top"),sQuery(id+"F22.wireOp",EDGE,"E43.MirrorCS"),sQuery(id+"F22.wireOp",EDGE,"E45.MirrorCS"),sQuery(id+"F22.wireOp",EDGE,"E46")])]});
            var Q7;
            Q7=makeQuery(id+"F25.opExtrude","SWEPT_BODY",BODY,{"disambiguationData":[OSD([sQuery(id+"F22.wireOp",EDGE,"E35.left"),sQuery(id+"F22.wireOp",EDGE,"E41.MirrorCS"),sQuery(id+"F22.wireOp",EDGE,"E44.MirrorCS"),sQuery(id+"F22.wireOp",EDGE,"E51.MirrorCS")])]});
            var Q8;
            Q8=makeQuery(id+"F25.opExtrude","SWEPT_BODY",BODY,{"disambiguationData":[OSD([sQuery(id+"F22.wireOp",EDGE,"E35.right"),sQuery(id+"F22.wireOp",EDGE,"E36"),sQuery(id+"F22.wireOp",EDGE,"E42.MirrorCS"),sQuery(id+"F22.wireOp",EDGE,"E47")])]});
            var Q9;
            Q9=makeQuery(id+"F27.opExtrude","SWEPT_BODY",BODY,{"disambiguationData":[OSD([sQuery(id+"F22.wireOp",EDGE,"E35.left"),sQuery(id+"F22.wireOp",EDGE,"E40.MirrorCS"),sQuery(id+"F22.wireOp",EDGE,"E41.MirrorCS"),sQuery(id+"F26.wireOp",EDGE,"E52"),sQuery(id+"F26.wireOp",EDGE,"E53")])]});
            var Q10;
            Q10=makeQuery(id+"F28.opPattern","COPY",BODY,{"derivedFrom":makeQuery(id+"F27.opExtrude","SWEPT_BODY",BODY,{"disambiguationData":[OSD([sQuery(id+"F22.wireOp",EDGE,"E35.left"),sQuery(id+"F22.wireOp",EDGE,"E40.MirrorCS"),sQuery(id+"F22.wireOp",EDGE,"E41.MirrorCS"),sQuery(id+"F26.wireOp",EDGE,"E52"),sQuery(id+"F26.wireOp",EDGE,"E53")])]}),"instanceName":"1"});
            var Q11;
            Q11=makeQuery(id+"F30.opExtrude","SWEPT_BODY",BODY,{"disambiguationData":[OSD([sQuery(id+"F29.wireOp",EDGE,"E54.bottom"),sQuery(id+"F29.wireOp",EDGE,"E54.top"),sQuery(id+"F29.wireOp",EDGE,"E54.left"),sQuery(id+"F29.wireOp",EDGE,"E54.right")])]});
            var Q12;
            Q12=makeQuery(id+"F32.opExtrude","SWEPT_BODY",BODY,{"disambiguationData":[OSD([sQuery(id+"F31.wireOp",EDGE,"E55.bottom"),sQuery(id+"F31.wireOp",EDGE,"E55.top"),sQuery(id+"F31.wireOp",EDGE,"E55.left"),sQuery(id+"F31.wireOp",EDGE,"E55.right")])]});
            var Q13;
            Q13=makeQuery(id+"F32.opExtrude","SWEPT_BODY",BODY,{"disambiguationData":[OSD([sQuery(id+"F31.wireOp",EDGE,"E56.MirrorCS"),sQuery(id+"F31.wireOp",EDGE,"E57.MirrorCS"),sQuery(id+"F31.wireOp",EDGE,"E58.MirrorCS"),sQuery(id+"F31.wireOp",EDGE,"E59.MirrorCS")])]});
            var Q14;
            Q14=makeQuery(id+"F34.opExtrude","SWEPT_BODY",BODY,{"disambiguationData":[OSD([sQuery(id+"F33.wireOp",EDGE,"E60.bottom"),sQuery(id+"F33.wireOp",EDGE,"E60.top"),sQuery(id+"F33.wireOp",EDGE,"E60.left"),sQuery(id+"F33.wireOp",EDGE,"E60.right")])]});
            var Q15;
            Q15=makeQuery(id+"F34.opExtrude","SWEPT_BODY",BODY,{"disambiguationData":[OSD([sQuery(id+"F22.wireOp",EDGE,"E35.bottom"),sQuery(id+"F22.wireOp",EDGE,"E35.top"),sQuery(id+"F33.wireOp",EDGE,"E61.MirrorCS"),sQuery(id+"F33.wireOp",EDGE,"E62.MirrorCS")])]});
            var Q16;
            Q16=makeQuery(id+"F36.opExtrude","SWEPT_BODY",BODY,{"disambiguationData":[OSD([sQuery(id+"F35.wireOp",EDGE,"E63.bottom"),sQuery(id+"F35.wireOp",EDGE,"E63.top"),sQuery(id+"F35.wireOp",EDGE,"E63.left"),sQuery(id+"F35.wireOp",EDGE,"E63.right")])]});
            var Q17;
            Q17=makeQuery(id+"F39.opPattern","COPY",BODY,{"derivedFrom":makeQuery(id+"F36.opExtrude","SWEPT_BODY",BODY,{"disambiguationData":[OSD([sQuery(id+"F35.wireOp",EDGE,"E63.bottom"),sQuery(id+"F35.wireOp",EDGE,"E63.top"),sQuery(id+"F35.wireOp",EDGE,"E63.left"),sQuery(id+"F35.wireOp",EDGE,"E63.right")])]}),"instanceName":"1"});
            var Q18;
            Q18=makeQuery(id+"F40.opPattern","COPY",BODY,{"derivedFrom":makeQuery(id+"F36.opExtrude","SWEPT_BODY",BODY,{"disambiguationData":[OSD([sQuery(id+"F35.wireOp",EDGE,"E63.bottom"),sQuery(id+"F35.wireOp",EDGE,"E63.top"),sQuery(id+"F35.wireOp",EDGE,"E63.left"),sQuery(id+"F35.wireOp",EDGE,"E63.right")])]}),"instanceName":"1"});
            var Q19;
            Q19=makeQuery(id+"F40.opPattern","COPY",BODY,{"derivedFrom":makeQuery(id+"F39.opPattern","COPY",BODY,{"derivedFrom":makeQuery(id+"F36.opExtrude","SWEPT_BODY",BODY,{"disambiguationData":[OSD([sQuery(id+"F35.wireOp",EDGE,"E63.bottom"),sQuery(id+"F35.wireOp",EDGE,"E63.top"),sQuery(id+"F35.wireOp",EDGE,"E63.left"),sQuery(id+"F35.wireOp",EDGE,"E63.right")])]}),"instanceName":"1"}),"instanceName":"1"});
            deleteBodies(context, id + "F41", {"entities" : qUnion([Q0, Q1, Q2, Q3, Q4, Q5, Q6, Q7, Q8, Q9, Q10, Q11, Q12, Q13, Q14, Q15, Q16, Q17, Q18, Q19])});
        }
    });
